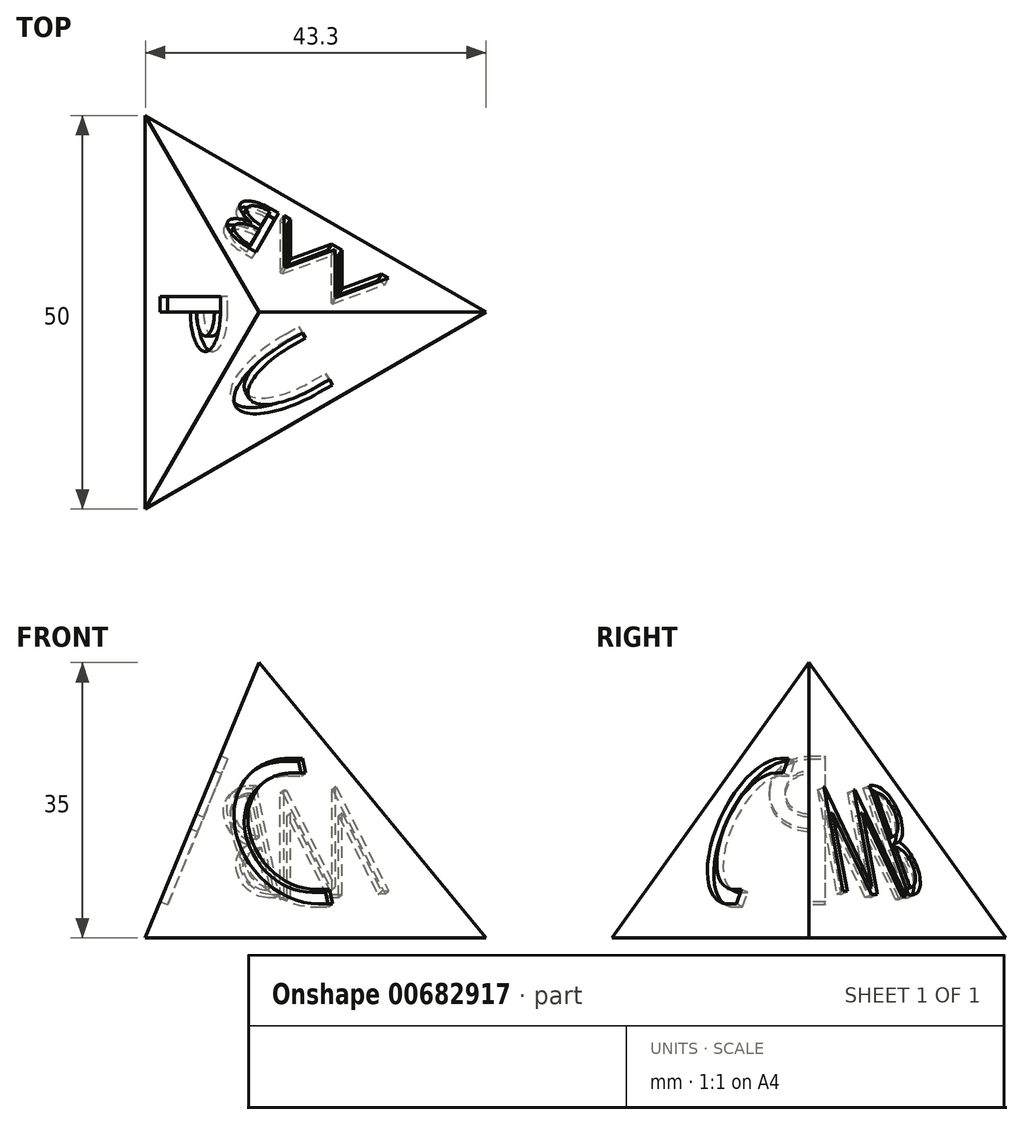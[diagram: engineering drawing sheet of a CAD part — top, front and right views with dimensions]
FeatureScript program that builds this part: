
annotation { "Feature Type Name" : "Feature", "Feature Type Description" : "" }
export const myFeature = defineFeature(function(context is Context, id is Id, definition is map)
    precondition{}
    {
        {
            var Q0;
            Q0=qCreatedBy(makeId("Top.planeOp"),FACE);
            var sketch = newSketch(context, id + "F0", { "sketchPlane" : qUnion([Q0])});
            skCircle(sketch, "E0.cCircle", {"center": v(0, 0) * mm, "radius": 14.43 * mm, "construction": true});
            skLineSegment(sketch, "E0.0", {"start": v(-14.43, -25) * mm, "end": v(-14.43, 25) * mm});
            skLineSegment(sketch, "E0.1", {"start": v(-14.43, 25) * mm, "end": v(28.87, 0) * mm});
            skLineSegment(sketch, "E0.2", {"start": v(28.87, 0) * mm, "end": v(-14.43, -25) * mm});
            skPoint(sketch, "E0.0.midPoint", {"position": v(-14.43, 0) * mm});
            skSolve(sketch);
        }
        {
            var Q0;
            Q0=makeQuery(id+"F0.imprint","IMPRINT",FACE,{"disambiguationData":[TD([[makeQuery(id+"F0.imprint","IMPRINT",EDGE,{"derivedFrom":sQuery(id+"F0.wireOp",EDGE,"E0.0")}),-1.0]])]});
            cPlane(context, id + "F1", {"entities" : qUnion([Q0]), "cplaneType" : CPlaneType.OFFSET, "offset" : 35 * mm, "width" : 150 * mm, "height" : 150 * mm});
        }
        {
            var Q0;
            Q0=qCreatedBy(id+"F1.planeOp",FACE);
            var sketch = newSketch(context, id + "F2", { "sketchPlane" : qUnion([Q0])});
            skPoint(sketch, "E1", {"position": v(0, 0) * mm});
            skSolve(sketch);
        }
        {
            var Q0;
            Q0=makeQuery(id+"F0.imprint","IMPRINT",FACE,{"disambiguationData":[TD([[makeQuery(id+"F0.imprint","IMPRINT",EDGE,{"derivedFrom":sQuery(id+"F0.wireOp",EDGE,"E0.0")}),-1.0]])]});
            var Q1;
            Q1=sQuery(id+"F2.wireOp",VERTEX,"E1");
            loft(context, id + "F3", {"sheetProfilesArray" : [{ "sheetProfileEntities" : qUnion([Q0]) }, { "sheetProfileEntities" : qUnion([Q1]) }]});
        }
        {
            var Q0;
            {var subQ0=sQuery(id+"F0.wireOp",EDGE,"E0.0");var subQ1=sQuery(id+"F0.wireOp",EDGE,"E0.1");var subQ2=sQuery(id+"F0.wireOp",EDGE,"E0.2");Q0=makeQuery(id+"F3.opLoft","SWEPT_FACE",FACE,{"disambiguationData":[OSD([subQ0,subQ1,subQ2]),TDD([makeQuery(id+"F0.imprint","INTERSECT",VERTEX,{"derivedFrom":[subQ0,subQ2]}),makeQuery(id+"F0.imprint","INTERSECT",VERTEX,{"derivedFrom":[subQ0,subQ1]}),makeQuery(id+"F0.imprint","IMPRINT",EDGE,{"derivedFrom":subQ0})])]});}
            var sketch = newSketch(context, id + "F4", { "sketchPlane" : qUnion([Q0])});
            skLineSegment(sketch, "E2", {"start": v(0, -5.5) * mm, "end": v(0, 32.36) * mm});
            skLineSegment(sketch, "E3", {"start": v(0, 9.5) * mm, "end": v(0, 19.5) * mm});
            skLineSegment(sketch, "E4", {"start": v(0, 23.78) * mm, "end": v(0, 32.36) * mm});
            skArc(sketch, "E5", {"start": v(0, 9.5) * mm, "mid": v(5, 14.5) * mm, "end": v(0, 19.5) * mm});
            skLineSegment(sketch, "E6", {"start": v(0, 19.5) * mm, "end": v(-2, 19.5) * mm});
            skLineSegment(sketch, "E7", {"start": v(-2, 19.5) * mm, "end": v(-2, -0.5) * mm});
            skLineSegment(sketch, "E8", {"start": v(-2, -0.5) * mm, "end": v(0, -0.5) * mm});
            skLineSegment(sketch, "E9", {"start": v(0, -0.5) * mm, "end": v(0, 9.5) * mm});
            skLineSegment(sketch, "E10", {"start": v(0, 19.5) * mm, "end": v(0, 17.5) * mm, "construction": true});
            skArc(sketch, "E11", {"start": v(0, 17.5) * mm, "mid": v(3, 14.5) * mm, "end": v(0, 11.5) * mm});
            skLineSegment(sketch, "E12", {"start": v(0, 17.5) * mm, "end": v(0, 11.5) * mm});
            skSolve(sketch);
        }
        {
            var Q0;
            {var subQ0=sQuery(id+"F4.wireOp",EDGE,"E6");Q0=makeQuery(id+"F4.imprint","IMPRINT",FACE,{"disambiguationData":[TD([[makeQuery(id+"F4.imprint","IMPRINT",EDGE,{"derivedFrom":subQ0}),1.0]])]});}
            var Q1;
            {var subQ0=sQuery(id+"F4.wireOp",EDGE,"E5");Q1=makeQuery(id+"F4.imprint","IMPRINT",FACE,{"disambiguationData":[TD([[makeQuery(id+"F4.imprint","IMPRINT",EDGE,{"derivedFrom":subQ0}),1.0]])]});}
            extrude(context, id + "F5", {"entities" : qUnion([Q0, Q1]), "operationType" : NewBodyOperationType.REMOVE, "oppositeDirection" : true, "depth" : 1 * mm, "offsetDistance" : 25 * mm});
        }
        {
            var Q0;
            {var subQ0=sQuery(id+"F0.wireOp",EDGE,"E0.2");var subQ1=sQuery(id+"F0.wireOp",EDGE,"E0.1");var subQ2=sQuery(id+"F0.wireOp",EDGE,"E0.0");Q0=makeQuery(id+"F3.opLoft","SWEPT_FACE",FACE,{"disambiguationData":[OSD([subQ2,subQ1,subQ0]),TDD([makeQuery(id+"F0.imprint","INTERSECT",VERTEX,{"derivedFrom":[subQ2,subQ0]}),makeQuery(id+"F0.imprint","INTERSECT",VERTEX,{"derivedFrom":[subQ1,subQ0]}),makeQuery(id+"F0.imprint","IMPRINT",EDGE,{"derivedFrom":subQ0})])]});}
            var sketch = newSketch(context, id + "F6", { "sketchPlane" : qUnion([Q0])});
            skLineSegment(sketch, "E13", {"start": v(1.18, -5.37) * mm, "end": v(0.1, -0.5) * mm, "construction": true});
            skLineSegment(sketch, "E14", {"start": v(0.1, -0.5) * mm, "end": v(-4.2, 19.04) * mm, "construction": true});
            skArc(sketch, "E15", {"start": v(-2.7, 19.04) * mm, "mid": v(-10.3, 7.13) * mm, "end": v(1.6, -0.5) * mm});
            skLineSegment(sketch, "E16", {"start": v(-2.7, 19.04) * mm, "end": v(-0.74, 19.47) * mm});
            skLineSegment(sketch, "E17", {"start": v(1.6, -0.5) * mm, "end": v(3.56, -0.06) * mm});
            skLineSegment(sketch, "E18.0", {"start": v(1.18, 1.46) * mm, "end": v(3.13, 1.9) * mm});
            skArc(sketch, "E18.1", {"start": v(-2.26, 17.09) * mm, "mid": v(-8.35, 7.56) * mm, "end": v(1.18, 1.46) * mm});
            skLineSegment(sketch, "E18.2", {"start": v(-2.26, 17.09) * mm, "end": v(-0.3, 17.52) * mm});
            skLineSegment(sketch, "E19", {"start": v(-0.74, 19.47) * mm, "end": v(-0.3, 17.52) * mm});
            skLineSegment(sketch, "E20", {"start": v(3.56, -0.06) * mm, "end": v(3.13, 1.9) * mm});
            skSolve(sketch);
        }
        {
            var Q0;
            Q0=makeQuery(id+"F6.imprint","IMPRINT",FACE,{"disambiguationData":[TD([[makeQuery(id+"F6.imprint","IMPRINT",EDGE,{"derivedFrom":sQuery(id+"F6.wireOp",EDGE,"E15")}),1.0]])]});
            extrude(context, id + "F7", {"entities" : qUnion([Q0]), "operationType" : NewBodyOperationType.REMOVE, "oppositeDirection" : true, "depth" : 1 * mm, "offsetDistance" : 25 * mm});
        }
        {
            var Q0;
            {var subQ0=sQuery(id+"F0.wireOp",EDGE,"E0.1");var subQ1=sQuery(id+"F0.wireOp",EDGE,"E0.2");var subQ2=sQuery(id+"F0.wireOp",EDGE,"E0.0");Q0=makeQuery(id+"F3.opLoft","SWEPT_FACE",FACE,{"disambiguationData":[OSD([subQ2,subQ0,subQ1]),TDD([makeQuery(id+"F0.imprint","INTERSECT",VERTEX,{"derivedFrom":[subQ2,subQ0]}),makeQuery(id+"F0.imprint","INTERSECT",VERTEX,{"derivedFrom":[subQ0,subQ1]}),makeQuery(id+"F0.imprint","IMPRINT",EDGE,{"derivedFrom":subQ0})])]});}
            var sketch = newSketch(context, id + "F8", { "sketchPlane" : qUnion([Q0])});
            skLineSegment(sketch, "E21", {"start": v(2.32, -5.37) * mm, "end": v(3.4, -0.5) * mm, "construction": true});
            skLineSegment(sketch, "E22", {"start": v(3.4, -0.5) * mm, "end": v(3.4, 14.5) * mm});
            skLineSegment(sketch, "E23", {"start": v(-4.1, 16.52) * mm, "end": v(-11.6, 3.53) * mm});
            skLineSegment(sketch, "E24.0", {"start": v(-4.96, 13.04) * mm, "end": v(-10.6, 3.28) * mm});
            skLineSegment(sketch, "E24.3", {"start": v(2.4, -0.27) * mm, "end": v(2.4, 11.44) * mm});
            skLineSegment(sketch, "E25", {"start": v(-4.18, 1.46) * mm, "end": v(-4.96, 1.63) * mm});
            skLineSegment(sketch, "E26", {"start": v(-4.18, 1.46) * mm, "end": v(-3.46, 1.3) * mm});
            skLineSegment(sketch, "E27", {"start": v(-4.96, 1.63) * mm, "end": v(-4.96, 13.04) * mm});
            skLineSegment(sketch, "E28", {"start": v(-3.46, 1.3) * mm, "end": v(2.4, 11.44) * mm});
            skLineSegment(sketch, "E29", {"start": v(-4.18, 1.46) * mm, "end": v(-3.96, 2.44) * mm, "construction": true});
            skLineSegment(sketch, "E30", {"start": v(-4.1, 16.52) * mm, "end": v(-3.96, 16.49) * mm});
            skLineSegment(sketch, "E31", {"start": v(3.4, 14.5) * mm, "end": v(3.04, 14.57) * mm});
            skLineSegment(sketch, "E32", {"start": v(-3.96, 16.49) * mm, "end": v(-3.96, 2.44) * mm});
            skLineSegment(sketch, "E33", {"start": v(3.04, 14.57) * mm, "end": v(-3.96, 2.44) * mm});
            skLineSegment(sketch, "E34", {"start": v(-11.6, 3.53) * mm, "end": v(-10.6, 3.28) * mm});
            skLineSegment(sketch, "E35", {"start": v(2.4, -0.27) * mm, "end": v(3.4, -0.5) * mm});
            skLineSegment(sketch, "E36", {"start": v(5.37, 0.3) * mm, "end": v(8.16, 13) * mm});
            skLineSegment(sketch, "E37", {"start": v(7.16, 13) * mm, "end": v(5.77, 6.64) * mm});
            skLineSegment(sketch, "E38", {"start": v(8.38, 13.97) * mm, "end": v(7.4, 14.19) * mm});
            skLineSegment(sketch, "E39", {"start": v(7.4, 14.19) * mm, "end": v(4.18, -0.46) * mm});
            skLineSegment(sketch, "E40", {"start": v(4.18, -0.46) * mm, "end": v(5.15, -0.68) * mm});
            skLineSegment(sketch, "E41", {"start": v(6.07, 3.47) * mm, "end": v(5.96, 2.98) * mm});
            skArc(sketch, "E42", {"start": v(5.37, 0.3) * mm, "mid": v(8.65, 2.4) * mm, "end": v(6.55, 5.67) * mm});
            skLineSegment(sketch, "E43", {"start": v(6.55, 5.67) * mm, "end": v(6.77, 6.65) * mm});
            skArc(sketch, "E44.0", {"start": v(5.15, -0.68) * mm, "mid": v(9.62, 2.18) * mm, "end": v(6.77, 6.65) * mm});
            skLineSegment(sketch, "E45.0", {"start": v(31.23, -17.63) * mm, "end": v(8.9, 40.46) * mm});
            skLineSegment(sketch, "E45.1", {"start": v(-35.75, -2.89) * mm, "end": v(31.23, -17.63) * mm});
            skLineSegment(sketch, "E45.2", {"start": v(8.9, 40.46) * mm, "end": v(-35.75, -2.89) * mm});
            skPoint(sketch, "E46.startSnap0", {"position": v(6.66, 6.16) * mm});
            skLineSegment(sketch, "E47", {"start": v(6.66, 6.16) * mm, "end": v(8.16, 13) * mm});
            skLineSegment(sketch, "E48", {"start": v(7.41, 9.58) * mm, "end": v(7.52, 10.06) * mm});
            skArc(sketch, "E49", {"start": v(8.16, 13) * mm, "mid": v(10.45, 9.42) * mm, "end": v(6.87, 7.13) * mm});
            skArc(sketch, "E50.0", {"start": v(8.38, 13.97) * mm, "mid": v(11.43, 9.2) * mm, "end": v(6.66, 6.16) * mm});
            skSolve(sketch);
        }
        {
            var Q0;
            Q0=makeQuery(id+"F8.imprint","IMPRINT",FACE,{"disambiguationData":[TD([[makeQuery(id+"F8.imprint","IMPRINT",EDGE,{"derivedFrom":sQuery(id+"F8.wireOp",EDGE,"E22")}),1.0]])]});
            var Q1;
            {var subQ10=sQuery(id+"F8.wireOp",EDGE,"E38");Q1=makeQuery(id+"F8.imprint","IMPRINT",FACE,{"disambiguationData":[TD([[makeQuery(id+"F8.imprint","IMPRINT",EDGE,{"derivedFrom":subQ10}),1.0]])]});}
            var Q2;
            {var subQ0=sQuery(id+"F8.wireOp",EDGE,"E47");var subQ1=sQuery(id+"F8.wireOp",EDGE,"E44.0");var subQ2=makeQuery(id+"F8.imprint","INTERSECT",VERTEX,{"derivedFrom":[subQ1,subQ0]});Q2=makeQuery(id+"F8.imprint","IMPRINT",FACE,{"disambiguationData":[TD([[makeQuery(id+"F8.imprint","IMPRINT",EDGE,{"disambiguationData":[TD([[subQ2,1.0]])],"derivedFrom":subQ1}),1.0]])]});}
            extrude(context, id + "F9", {"entities" : qUnion([Q0, Q1, Q2]), "operationType" : NewBodyOperationType.REMOVE, "oppositeDirection" : true, "depth" : 1 * mm, "offsetDistance" : 25 * mm});
        }
    });
